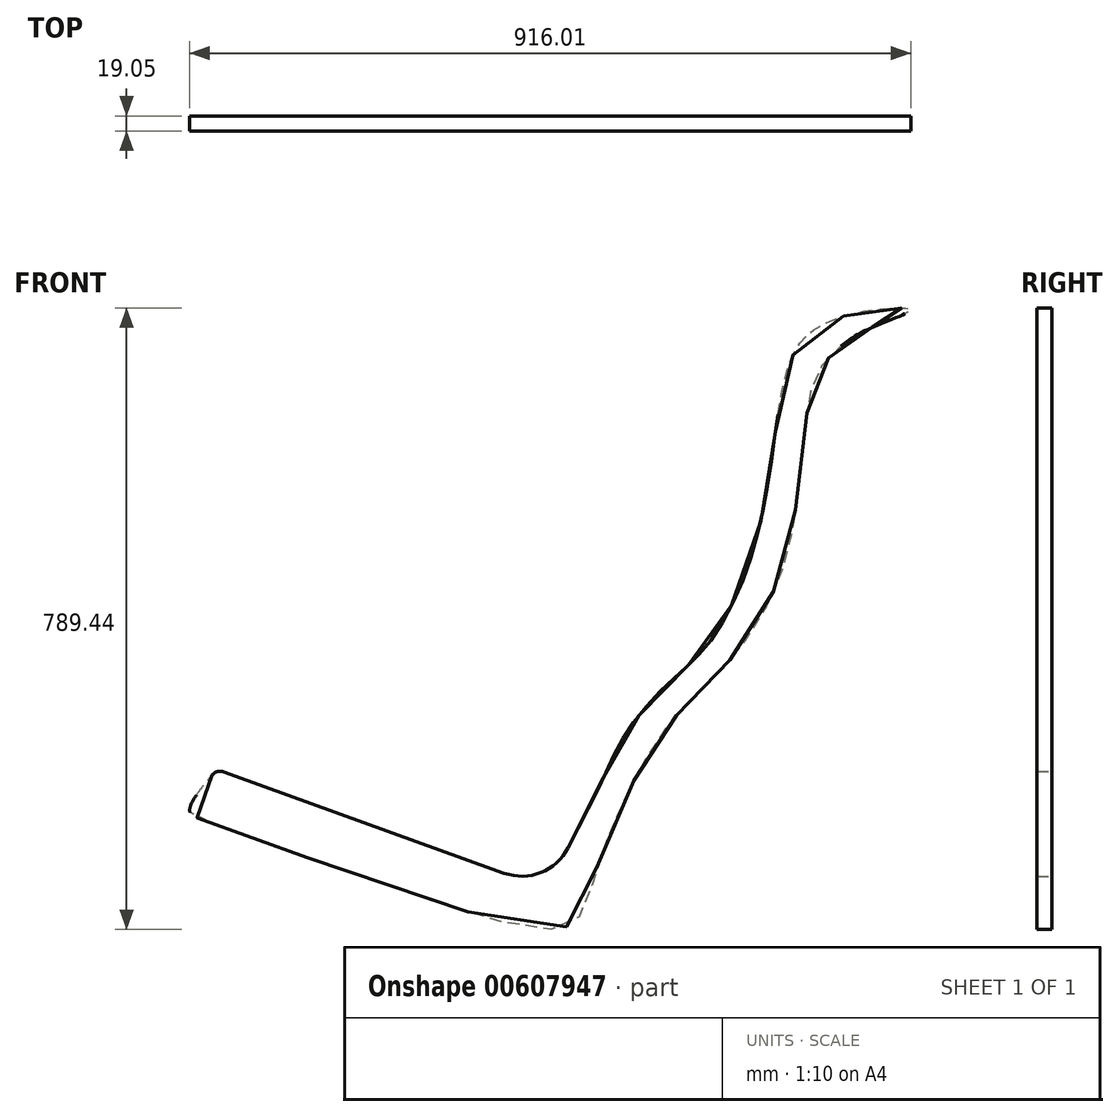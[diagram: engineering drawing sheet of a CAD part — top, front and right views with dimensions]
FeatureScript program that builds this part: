
annotation { "Feature Type Name" : "Feature", "Feature Type Description" : "" }
export const myFeature = defineFeature(function(context is Context, id is Id, definition is map)
    precondition{}
    {
        {
            var Q0;
            Q0=qCreatedBy(makeId("Front.planeOp"),FACE);
            var sketch = newSketch(context, id + "F0", { "sketchPlane" : qUnion([Q0])});
            skLineSegment(sketch, "E0", {"start": v(-325.68, 35.82) * mm, "end": v(330, -43.04) * mm, "construction": true});
            skLineSegment(sketch, "E1", {"start": v(-332.32, -90.5) * mm, "end": v(24.39, -219.2) * mm});
            skArc(sketch, "E2", {"start": v(24.39, -219.2) * mm, "mid": v(71.07, -218.45) * mm, "end": v(105.53, -186.96) * mm});
            skFitSpline(sketch, "E3", {"points": [v(105.53, -186.96) * mm, v(148, -102.73) * mm, v(182.88, -35.88) * mm, v(237.1, 25.67) * mm, v(282.75, 71) * mm, v(331.72, 163.8) * mm, v(360.8, 283.67) * mm, v(378.05, 396.46) * mm, v(407.35, 462.36) * mm, v(463.1, 490.61) * mm, v(511.3, 497.84) * mm, v(540.9, 496.56) * mm, v(491.07, 473.83) * mm, v(453.98, 451.41) * mm, v(423.21, 418.4) * mm, v(408.5, 360.91) * mm, v(390.52, 217.34) * mm, v(359.62, 123.84) * mm, v(302.84, 41.8) * mm, v(241.42, -21.1) * mm, v(191.95, -95.96) * mm, v(140.75, -216.97) * mm, v(111.75, -282.68) * mm, v(-15.03, -270.75) * mm, v(-347.14, -155.93) * mm, v(-375.1, -139.15) * mm, v(-340.65, -87.5) * mm], "startDerivative": vector(1105.47, 2132.24) * mm, "endDerivative": vector(1571.17, 1863.8) * mm});
            skArc(sketch, "E4.filletArc", {"start": v(-332.32, -90.5) * mm, "mid": v(-339.94, -90.2) * mm, "end": v(-346.37, -94.3) * mm});
            skSolve(sketch);
        }
        {
            var Q0;
            Q0 = qSketchRegion(id + "F0", true);
            extrude(context, id + "F1", {"entities" : qUnion([Q0]), "depth" : 19.05 * mm, "offsetDistance" : 25.4 * mm});
        }
    });
